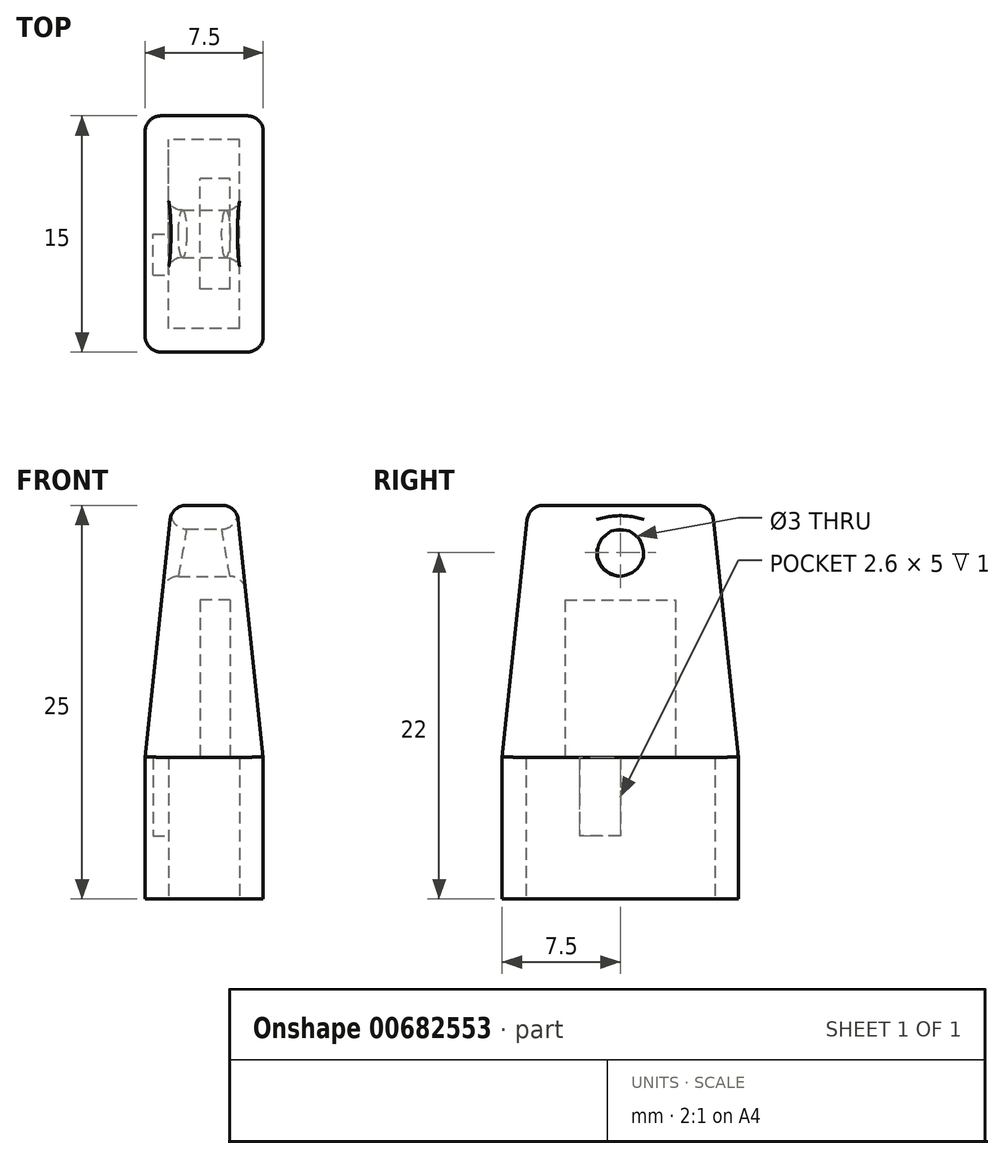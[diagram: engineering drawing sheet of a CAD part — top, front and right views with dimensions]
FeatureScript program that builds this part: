
annotation { "Feature Type Name" : "Feature", "Feature Type Description" : "" }
export const myFeature = defineFeature(function(context is Context, id is Id, definition is map)
    precondition{}
    {
        {
            var Q0;
            Q0=qCreatedBy(makeId("Top.planeOp"),FACE);
            var sketch = newSketch(context, id + "F0", { "sketchPlane" : qUnion([Q0])});
            skLineSegment(sketch, "E0.bottom", {"start": v(2.25, -6) * mm, "end": v(-2.25, -6) * mm});
            skLineSegment(sketch, "E0.top", {"start": v(2.25, 6) * mm, "end": v(-2.25, 6) * mm});
            skLineSegment(sketch, "E0.left", {"start": v(2.25, -6) * mm, "end": v(2.25, 6) * mm});
            skLineSegment(sketch, "E0.right", {"start": v(-2.25, -6) * mm, "end": v(-2.25, 6) * mm});
            skPoint(sketch, "E0.middle", {"position": v(0, 0) * mm});
            skLineSegment(sketch, "E1.bottom", {"start": v(3.75, -7.5) * mm, "end": v(-3.75, -7.5) * mm});
            skLineSegment(sketch, "E1.top", {"start": v(3.75, 7.5) * mm, "end": v(-3.75, 7.5) * mm});
            skLineSegment(sketch, "E1.left", {"start": v(3.75, -7.5) * mm, "end": v(3.75, 7.5) * mm});
            skLineSegment(sketch, "E1.right", {"start": v(-3.75, -7.5) * mm, "end": v(-3.75, 7.5) * mm});
            skSolve(sketch);
        }
        {
            var Q0;
            Q0 = qSketchRegion(id + "F0", true);
            extrude(context, id + "F1", {"entities" : qUnion([Q0]), "depth" : 9 * mm, "offsetDistance" : 25 * mm});
        }
        {
            var Q0;
            Q0=makeQuery(id+"F1.opExtrude","CAP_FACE",FACE,{"disambiguationData":[OSD([sQuery(id+"F0.wireOp",EDGE,"E0.bottom"),sQuery(id+"F0.wireOp",EDGE,"E0.top"),sQuery(id+"F0.wireOp",EDGE,"E0.left"),sQuery(id+"F0.wireOp",EDGE,"E0.right"),sQuery(id+"F0.wireOp",EDGE,"E1.bottom"),sQuery(id+"F0.wireOp",EDGE,"E1.top"),sQuery(id+"F0.wireOp",EDGE,"E1.left"),sQuery(id+"F0.wireOp",EDGE,"E1.right")])],"isStart":false});
            var sketch = newSketch(context, id + "F2", { "sketchPlane" : qUnion([Q0])});
            skLineSegment(sketch, "E2.0", {"start": v(3.75, -7.5) * mm, "end": v(-3.75, -7.5) * mm});
            skLineSegment(sketch, "E3.0", {"start": v(-3.75, -7.5) * mm, "end": v(-3.75, 7.5) * mm});
            skLineSegment(sketch, "E4.0", {"start": v(3.75, 7.5) * mm, "end": v(-3.75, 7.5) * mm});
            skLineSegment(sketch, "E5.0", {"start": v(3.75, -7.5) * mm, "end": v(3.75, 7.5) * mm});
            skSolve(sketch);
        }
        {
            var Q0;
            Q0 = qSketchRegion(id + "F2", true);
            extrude(context, id + "F3", {"entities" : qUnion([Q0]), "operationType" : NewBodyOperationType.ADD, "depth" : 16 * mm, "offsetDistance" : 25 * mm, "hasDraft" : true, "draftAngle" : 6 * degree, "draftPullDirection" : true});
        }
        {
            var Q0;
            Q0=makeQuery(id+"F3.opExtrude","CAP_FACE",FACE,{"disambiguationData":[OSD([sQuery(id+"F2.wireOp",EDGE,"E2.0"),sQuery(id+"F2.wireOp",EDGE,"E3.0"),sQuery(id+"F2.wireOp",EDGE,"E4.0"),sQuery(id+"F2.wireOp",EDGE,"E5.0")])],"isStart":true});
            var sketch = newSketch(context, id + "F4", { "sketchPlane" : qUnion([Q0])});
            skLineSegment(sketch, "E6.bottom", {"start": v(1.65, 3.5) * mm, "end": v(-0.25, 3.5) * mm});
            skLineSegment(sketch, "E6.top", {"start": v(1.65, -3.5) * mm, "end": v(-0.25, -3.5) * mm});
            skLineSegment(sketch, "E6.left", {"start": v(1.65, 3.5) * mm, "end": v(1.65, -3.5) * mm});
            skLineSegment(sketch, "E6.right", {"start": v(-0.25, 3.5) * mm, "end": v(-0.25, -3.5) * mm});
            skLineSegment(sketch, "E7", {"start": v(0, 0) * mm, "end": v(7.06, 0) * mm, "construction": true});
            skPoint(sketch, "E7.endSnap0", {"position": v(-2.25, 0) * mm});
            skSolve(sketch);
        }
        {
            var Q0;
            Q0 = qSketchRegion(id + "F4", true);
            extrude(context, id + "F5", {"entities" : qUnion([Q0]), "operationType" : NewBodyOperationType.REMOVE, "oppositeDirection" : true, "depth" : 10 * mm, "offsetDistance" : 25 * mm});
        }
        {
            var Q0;
            Q0=qCreatedBy(makeId("Right.planeOp"),FACE);
            var sketch = newSketch(context, id + "F6", { "sketchPlane" : qUnion([Q0])});
            skLineSegment(sketch, "E8", {"start": v(0, 19.87) * mm, "end": v(0, 30.44) * mm, "construction": true});
            skLineSegment(sketch, "E9", {"start": v(2.8, 22) * mm, "end": v(-3.5, 22) * mm, "construction": true});
            skCircle(sketch, "E10", {"center": v(0, 22) * mm, "radius": 1.5 * mm});
            skSolve(sketch);
        }
        {
            var Q0;
            Q0 = qSketchRegion(id + "F6", true);
            extrude(context, id + "F7", {"entities" : qUnion([Q0]), "operationType" : NewBodyOperationType.REMOVE, "oppositeDirection" : true, "depth" : 25 * mm, "offsetDistance" : 25 * mm, "symmetric" : true});
        }
        {
            var Q0;
            Q0=makeQuery(id+"F3.opExtrude","SWEPT_EDGE",EDGE,{"disambiguationData":[OSD([sQuery(id+"F2.wireOp",EDGE,"E2.0"),sQuery(id+"F2.wireOp",EDGE,"E5.0")])]});
            var Q1;
            Q1=makeQuery(id+"F3.opExtrude","SWEPT_EDGE",EDGE,{"disambiguationData":[OSD([sQuery(id+"F2.wireOp",EDGE,"E4.0"),sQuery(id+"F2.wireOp",EDGE,"E5.0")])]});
            var Q2;
            Q2=makeQuery(id+"F3.opExtrude","SWEPT_EDGE",EDGE,{"disambiguationData":[OSD([sQuery(id+"F2.wireOp",EDGE,"E3.0"),sQuery(id+"F2.wireOp",EDGE,"E4.0")])]});
            var Q3;
            Q3=makeQuery(id+"F3.opExtrude","SWEPT_EDGE",EDGE,{"disambiguationData":[OSD([sQuery(id+"F2.wireOp",EDGE,"E2.0"),sQuery(id+"F2.wireOp",EDGE,"E3.0")])]});
            var Q4;
            Q4=makeQuery(id+"F3.opExtrude","CAP_FACE",FACE,{"disambiguationData":[OSD([sQuery(id+"F2.wireOp",EDGE,"E2.0"),sQuery(id+"F2.wireOp",EDGE,"E3.0"),sQuery(id+"F2.wireOp",EDGE,"E4.0"),sQuery(id+"F2.wireOp",EDGE,"E5.0")])],"isStart":false});
            var Q5;
            Q5=makeQuery(id+"F7.boolean.opBoolean","INTERSECT",EDGE,{"derivedFrom":[makeQuery(id+"F3.opExtrude","SWEPT_FACE",FACE,{"disambiguationData":[OSD([sQuery(id+"F2.wireOp",EDGE,"E5.0")])]}),makeQuery(id+"F7.opExtrude","SWEPT_FACE",FACE,{"disambiguationData":[OSD([sQuery(id+"F6.wireOp",EDGE,"E10")])]})]});
            var Q6;
            Q6=makeQuery(id+"F7.boolean.opBoolean","INTERSECT",EDGE,{"derivedFrom":[makeQuery(id+"F3.opExtrude","SWEPT_FACE",FACE,{"disambiguationData":[OSD([sQuery(id+"F2.wireOp",EDGE,"E3.0")])]}),makeQuery(id+"F7.opExtrude","SWEPT_FACE",FACE,{"disambiguationData":[OSD([sQuery(id+"F6.wireOp",EDGE,"E10")])]})]});
            var Q7;
            Q7=makeQuery(id+"F1.opExtrude","SWEPT_EDGE",EDGE,{"disambiguationData":[OSD([sQuery(id+"F0.wireOp",EDGE,"E1.bottom"),sQuery(id+"F0.wireOp",EDGE,"E1.right")])]});
            var Q8;
            Q8=makeQuery(id+"F1.opExtrude","SWEPT_EDGE",EDGE,{"disambiguationData":[OSD([sQuery(id+"F0.wireOp",EDGE,"E1.top"),sQuery(id+"F0.wireOp",EDGE,"E1.right")])]});
            var Q9;
            Q9=makeQuery(id+"F1.opExtrude","SWEPT_EDGE",EDGE,{"disambiguationData":[OSD([sQuery(id+"F0.wireOp",EDGE,"E1.top"),sQuery(id+"F0.wireOp",EDGE,"E1.left")])]});
            var Q10;
            Q10=makeQuery(id+"F1.opExtrude","SWEPT_EDGE",EDGE,{"disambiguationData":[OSD([sQuery(id+"F0.wireOp",EDGE,"E1.bottom"),sQuery(id+"F0.wireOp",EDGE,"E1.left")])]});
            fillet(context, id + "F8", {"entities" : qUnion([Q0, Q1, Q2, Q3, Q4, Q5, Q6, Q7, Q8, Q9, Q10]), "radius" : 1 * mm, "tangentPropagation" : true, "allowEdgeOverflow" : false});
        }
        {
            var Q0;
            Q0=makeQuery(id+"F1.opExtrude","SWEPT_FACE",FACE,{"disambiguationData":[OSD([sQuery(id+"F0.wireOp",EDGE,"E0.right")])]});
            var sketch = newSketch(context, id + "F9", { "sketchPlane" : qUnion([Q0])});
            skLineSegment(sketch, "E11", {"start": v(0, 0) * mm, "end": v(0, 11.9) * mm, "construction": true});
            skPoint(sketch, "E11.endSnap0", {"position": v(0, 9) * mm});
            skLineSegment(sketch, "E12.left", {"start": v(0, 9) * mm, "end": v(0, 4) * mm});
            skLineSegment(sketch, "E13.bottom", {"start": v(0, 9) * mm, "end": v(-2.6, 9) * mm});
            skLineSegment(sketch, "E13.top", {"start": v(0, 4) * mm, "end": v(-2.6, 4) * mm});
            skLineSegment(sketch, "E13.right", {"start": v(-2.6, 9) * mm, "end": v(-2.6, 4) * mm});
            skSolve(sketch);
        }
        {
            var Q0;
            Q0 = qSketchRegion(id + "F9", true);
            extrude(context, id + "F10", {"entities" : qUnion([Q0]), "operationType" : NewBodyOperationType.REMOVE, "oppositeDirection" : true, "depth" : 1 * mm, "offsetDistance" : 25 * mm});
        }
    });
